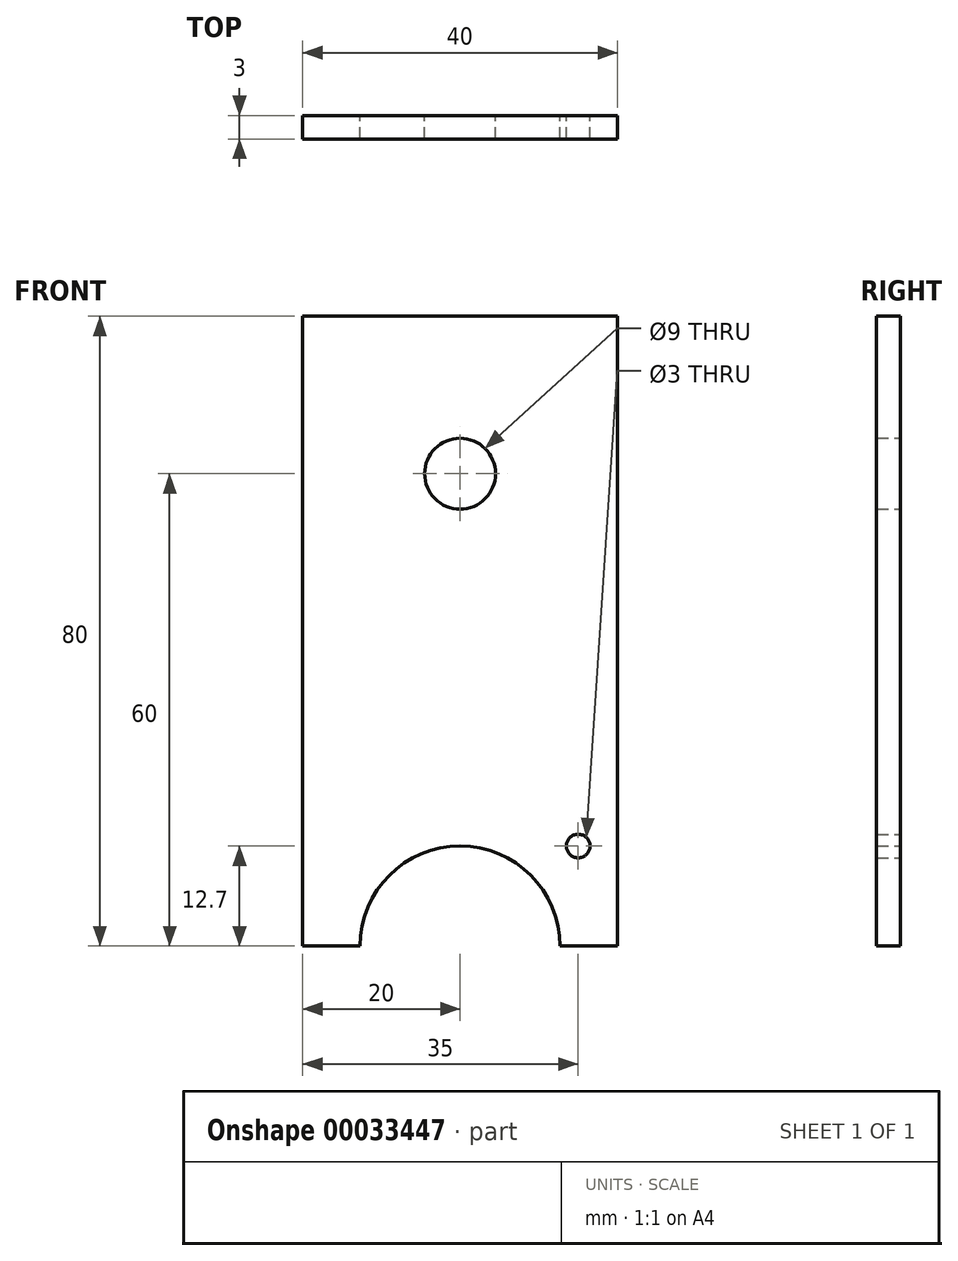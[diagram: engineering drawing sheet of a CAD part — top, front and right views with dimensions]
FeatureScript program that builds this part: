
annotation { "Feature Type Name" : "Feature", "Feature Type Description" : "" }
export const myFeature = defineFeature(function(context is Context, id is Id, definition is map)
    precondition{}
    {
        {
            var Q0;
            Q0=qCreatedBy(makeId("Front.planeOp"),FACE);
            var sketch = newSketch(context, id + "F0", { "sketchPlane" : qUnion([Q0])});
            skLineSegment(sketch, "E0.rect.bottom", {"start": v(-20, 40) * mm, "end": v(20, 40) * mm});
            skLineSegment(sketch, "E0.rect.top", {"start": v(-20, -40) * mm, "end": v(20, -40) * mm});
            skLineSegment(sketch, "E0.rect.left", {"start": v(-20, 40) * mm, "end": v(-20, -40) * mm});
            skLineSegment(sketch, "E0.rect.right", {"start": v(20, 40) * mm, "end": v(20, -40) * mm});
            skPoint(sketch, "E0.rect.middle", {"position": v(0, 0) * mm});
            skLineSegment(sketch, "E1", {"start": v(0, 49.3) * mm, "end": v(0, -50.45) * mm, "construction": true});
            skPoint(sketch, "E1.startSnap0", {"position": v(0, 40) * mm});
            skLineSegment(sketch, "E2.0", {"start": v(-20, -27.3) * mm, "end": v(20, -27.3) * mm, "construction": true});
            skLineSegment(sketch, "E3.0", {"start": v(-12.7, 49.3) * mm, "end": v(-12.7, -50.45) * mm, "construction": true});
            skLineSegment(sketch, "E4.0", {"start": v(12.7, 49.3) * mm, "end": v(12.7, -50.45) * mm, "construction": true});
            skArc(sketch, "E5", {"start": v(12.7, -40) * mm, "mid": v(0, -27.3) * mm, "end": v(-12.7, -40) * mm});
            skLineSegment(sketch, "E6.0", {"start": v(-20, 20) * mm, "end": v(20, 20) * mm, "construction": true});
            skLineSegment(sketch, "E7.0", {"start": v(-20, -20) * mm, "end": v(20, -20) * mm, "construction": true});
            skLineSegment(sketch, "E8.0", {"start": v(15, 40) * mm, "end": v(15, -40) * mm, "construction": true});
            skCircle(sketch, "E9", {"center": v(0, 20) * mm, "radius": 4.5 * mm});
            skCircle(sketch, "E10", {"center": v(15, -27.3) * mm, "radius": 1.5 * mm});
            skSolve(sketch);
        }
        {
            var Q0;
            Q0=makeQuery(id+"F0.imprint","IMPRINT",FACE,{"disambiguationData":[TD([[makeQuery(id+"F0.imprint","IMPRINT",EDGE,{"derivedFrom":sQuery(id+"F0.wireOp",EDGE,"E0.rect.bottom")}),-1.0]])]});
            extrude(context, id + "F1", {"entities" : qUnion([Q0]), "depth" : 3 * mm});
        }
    });
